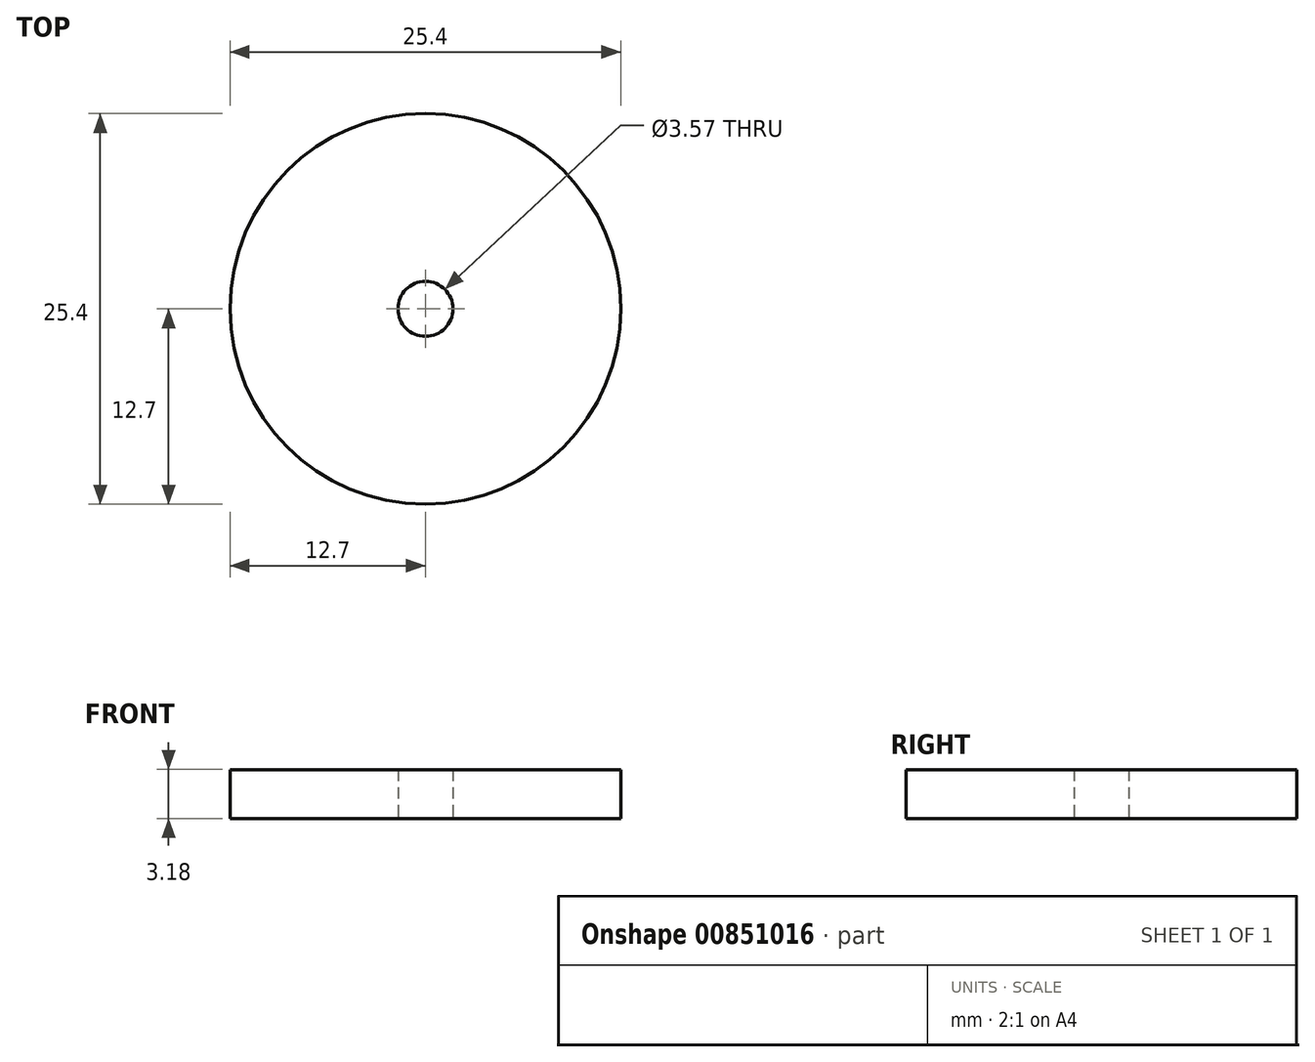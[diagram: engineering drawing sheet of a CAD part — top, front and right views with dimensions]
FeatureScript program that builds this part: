
annotation { "Feature Type Name" : "Feature", "Feature Type Description" : "" }
export const myFeature = defineFeature(function(context is Context, id is Id, definition is map)
    precondition{}
    {
        {
            var Q0;
            Q0=qCreatedBy(makeId("Top.planeOp"),FACE);
            var sketch = newSketch(context, id + "F0", { "sketchPlane" : qUnion([Q0])});
            skCircle(sketch, "E0", {"center": v(29.76, 36.59) * mm, "radius": 12.7 * mm});
            skCircle(sketch, "E1", {"center": v(29.76, 36.59) * mm, "radius": 1.79 * mm});
            skSolve(sketch);
        }
        {
            var Q0;
            Q0=makeQuery(id+"F0.imprint","IMPRINT",FACE,{"disambiguationData":[TD([[makeQuery(id+"F0.imprint","IMPRINT",EDGE,{"derivedFrom":sQuery(id+"F0.wireOp",EDGE,"E0")}),1.0]])]});
            extrude(context, id + "F1", {"entities" : qUnion([Q0]), "depth" : 3.17 * mm, "offsetDistance" : 25.4 * mm});
        }
    });
